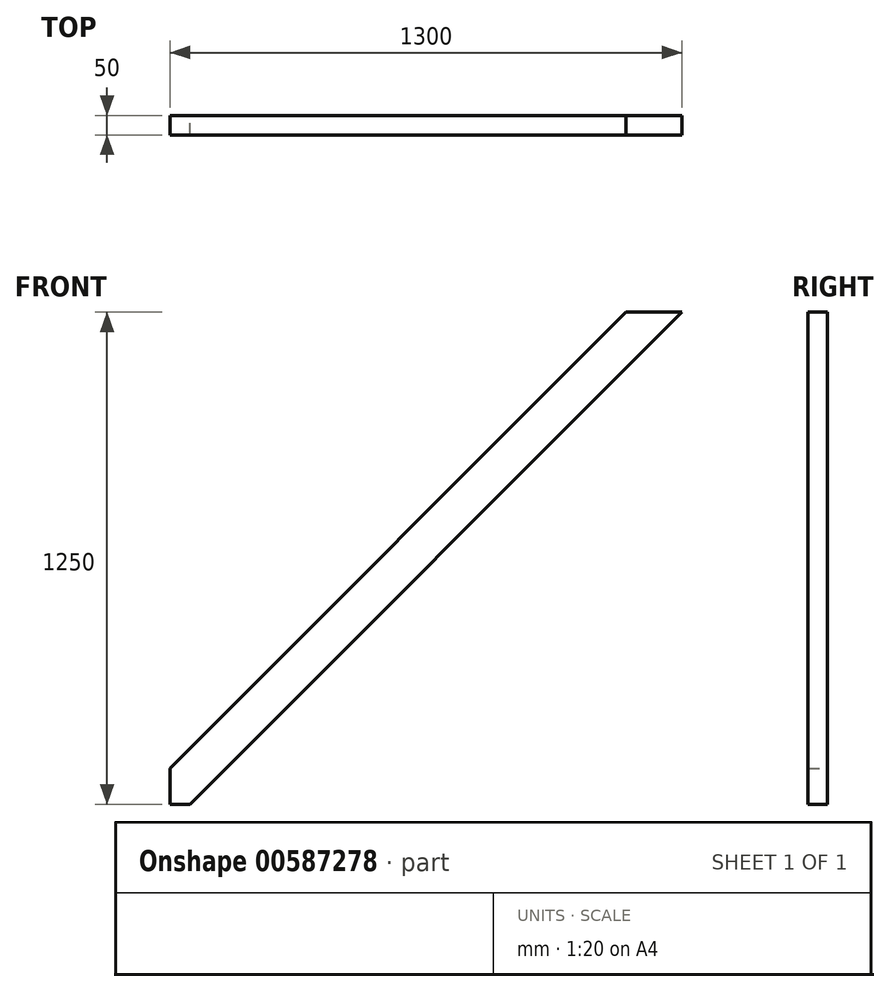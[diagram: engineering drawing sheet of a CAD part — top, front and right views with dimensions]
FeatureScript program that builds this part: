
annotation { "Feature Type Name" : "Feature", "Feature Type Description" : "" }
export const myFeature = defineFeature(function(context is Context, id is Id, definition is map)
    precondition{}
    {
        {
            var Q0;
            Q0=qCreatedBy(makeId("Front.planeOp"),FACE);
            var sketch = newSketch(context, id + "F0", { "sketchPlane" : qUnion([Q0])});
            skLineSegment(sketch, "E0", {"start": v(-1250, 0) * mm, "end": v(1250, 0) * mm, "construction": true});
            skLineSegment(sketch, "E1", {"start": v(1250, 0) * mm, "end": v(0, 1250) * mm, "construction": true});
            skLineSegment(sketch, "E2", {"start": v(0, 1250) * mm, "end": v(-1250, 0) * mm});
            skLineSegment(sketch, "E3", {"start": v(0, 1250) * mm, "end": v(-141.42, 1250) * mm});
            skLineSegment(sketch, "E4", {"start": v(-1250, 0) * mm, "end": v(-1300, 0) * mm});
            skLineSegment(sketch, "E5", {"start": v(-1300, 91.42) * mm, "end": v(-141.42, 1250) * mm});
            skLineSegment(sketch, "E6", {"start": v(-1300, 0) * mm, "end": v(-1300, 91.42) * mm});
            skSolve(sketch);
        }
        {
            var Q0;
            Q0=makeQuery(id+"F0.imprint","IMPRINT",FACE,{"disambiguationData":[TD([[makeQuery(id+"F0.imprint","IMPRINT",EDGE,{"derivedFrom":sQuery(id+"F0.wireOp",EDGE,"E2")}),-1.0]])]});
            extrude(context, id + "F1", {"entities" : qUnion([Q0]), "depth" : 50 * mm, "offsetDistance" : 25 * mm});
        }
    });
